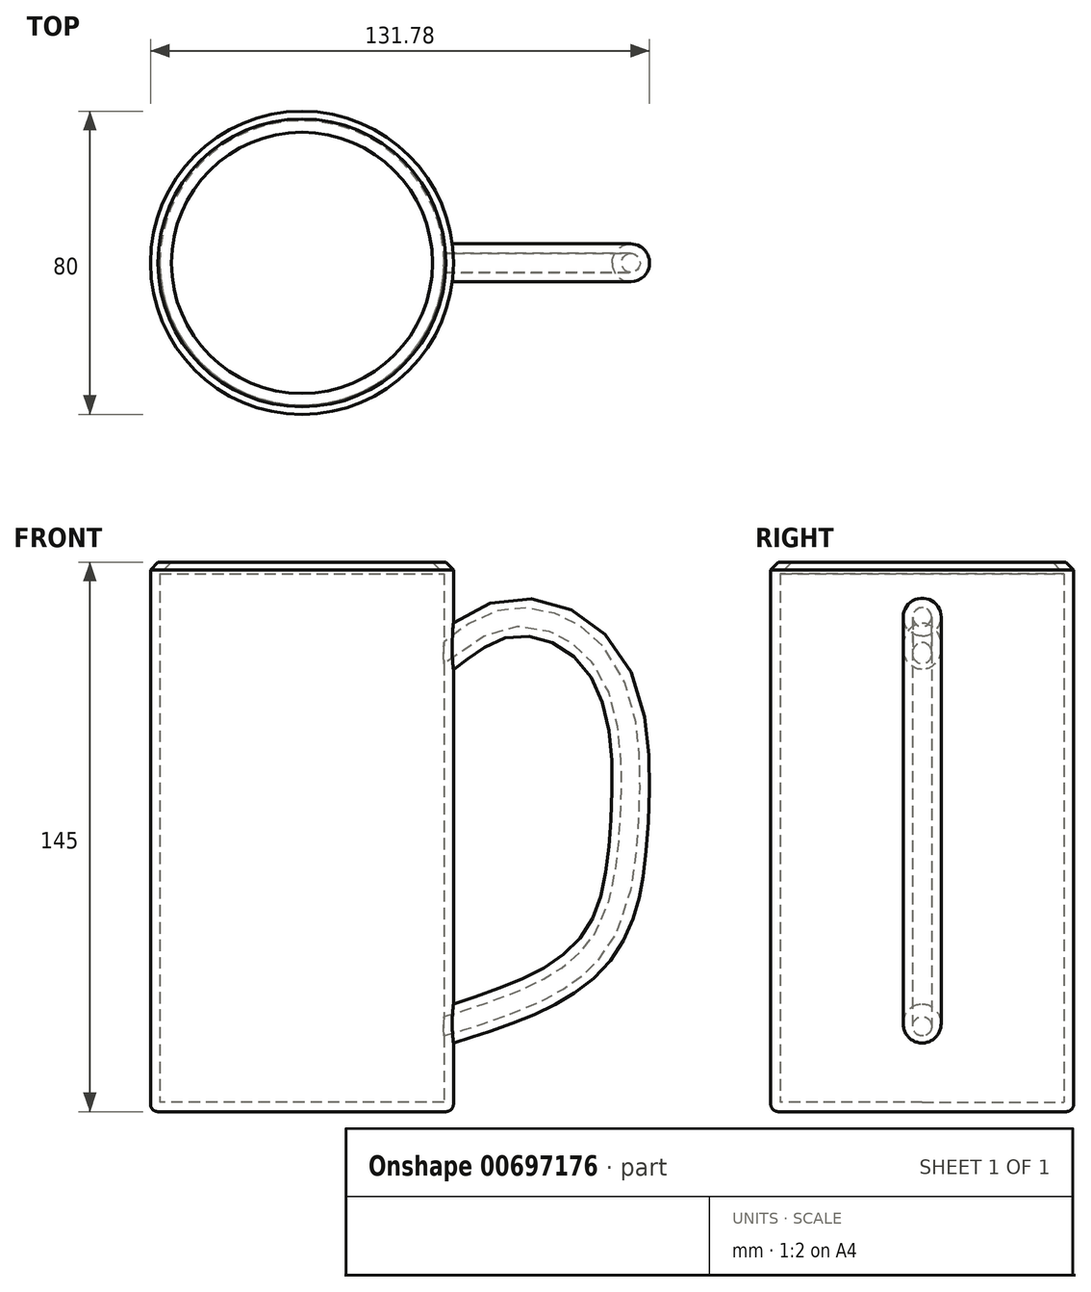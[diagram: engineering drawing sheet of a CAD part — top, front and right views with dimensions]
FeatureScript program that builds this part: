
annotation { "Feature Type Name" : "Feature", "Feature Type Description" : "" }
export const myFeature = defineFeature(function(context is Context, id is Id, definition is map)
    precondition{}
    {
        {
            var Q0;
            Q0=qCreatedBy(makeId("Top.planeOp"),FACE);
            var sketch = newSketch(context, id + "F0", { "sketchPlane" : qUnion([Q0])});
            skCircle(sketch, "E0", {"center": v(0, 0) * mm, "radius": 40 * mm});
            skSolve(sketch);
        }
        {
            var Q0;
            Q0 = qSketchRegion(id + "F0", true);
            extrude(context, id + "F1", {"entities" : qUnion([Q0]), "depth" : 145 * mm, "offsetDistance" : 25 * mm});
        }
        {
            var Q0;
            Q0=qCreatedBy(makeId("Front.planeOp"),FACE);
            var sketch = newSketch(context, id + "F2", { "sketchPlane" : qUnion([Q0])});
            skFitSpline(sketch, "E1", {"points": [v(27.98, 112.2) * mm, v(40.1, 112.47) * mm, v(54.72, 121.29) * mm, v(72.64, 113.3) * mm, v(77.6, 74.98) * mm, v(70.7, 48.51) * mm, v(48.38, 35.28) * mm, v(30.97, 30.06) * mm], "startDerivative": vector(118.34, -20.38) * mm, "endDerivative": vector(-37.75, -1.67) * mm});
            skSolve(sketch);
        }
        {
            var Q0;
            Q0=qCreatedBy(makeId("Right.planeOp"),FACE);
            cPlane(context, id + "F3", {"entities" : qUnion([Q0]), "cplaneType" : CPlaneType.OFFSET, "offset" : 27.6 * mm, "width" : 150 * mm, "height" : 150 * mm});
        }
        {
            var Q0;
            Q0=qCreatedBy(id+"F3.planeOp",FACE);
            var sketch = newSketch(context, id + "F4", { "sketchPlane" : qUnion([Q0])});
            skCircle(sketch, "E2", {"center": v(0, 121.15) * mm, "radius": 5 * mm});
            skSolve(sketch);
        }
        {
            var Q0;
            Q0 = qSketchRegion(id + "F4", true);
            var Q1;
            Q1 = qConstructionFilter(qBodyType(qCreatedBy(id + "F2" ,EDGE), BodyType.WIRE), ConstructionObject.NO);
            sweep(context, id + "F5", {"operationType" : NewBodyOperationType.ADD, "profiles" : qUnion([Q0]), "path" : qUnion([Q1])});
        }
        {
            var Q0;
            Q0=makeQuery(id+"F1.opExtrude","CAP_FACE",FACE,{"disambiguationData":[OSD([sQuery(id+"F0.wireOp",EDGE,"E0")])],"isStart":false});
            chamfer(context, id + "F6", {"entities" : qUnion([Q0]), "width" : 2 * mm, "tangentPropagation" : true});
        }
        {
            var Q0;
            Q0=makeQuery(id+"F1.opExtrude","CAP_FACE",FACE,{"disambiguationData":[OSD([sQuery(id+"F0.wireOp",EDGE,"E0")])],"isStart":true});
            fillet(context, id + "F7", {"entities" : qUnion([Q0]), "radius" : 2 * mm, "tangentPropagation" : true, "allowEdgeOverflow" : false});
        }
        {
            var Q0;
            Q0=makeQuery(id+"F1.opExtrude","CAP_FACE",FACE,{"disambiguationData":[OSD([sQuery(id+"F0.wireOp",EDGE,"E0")])],"isStart":false});
            shell(context, id + "F8", {"entities" : qUnion([Q0]), "thickness" : 2.5 * mm});
        }
    });
